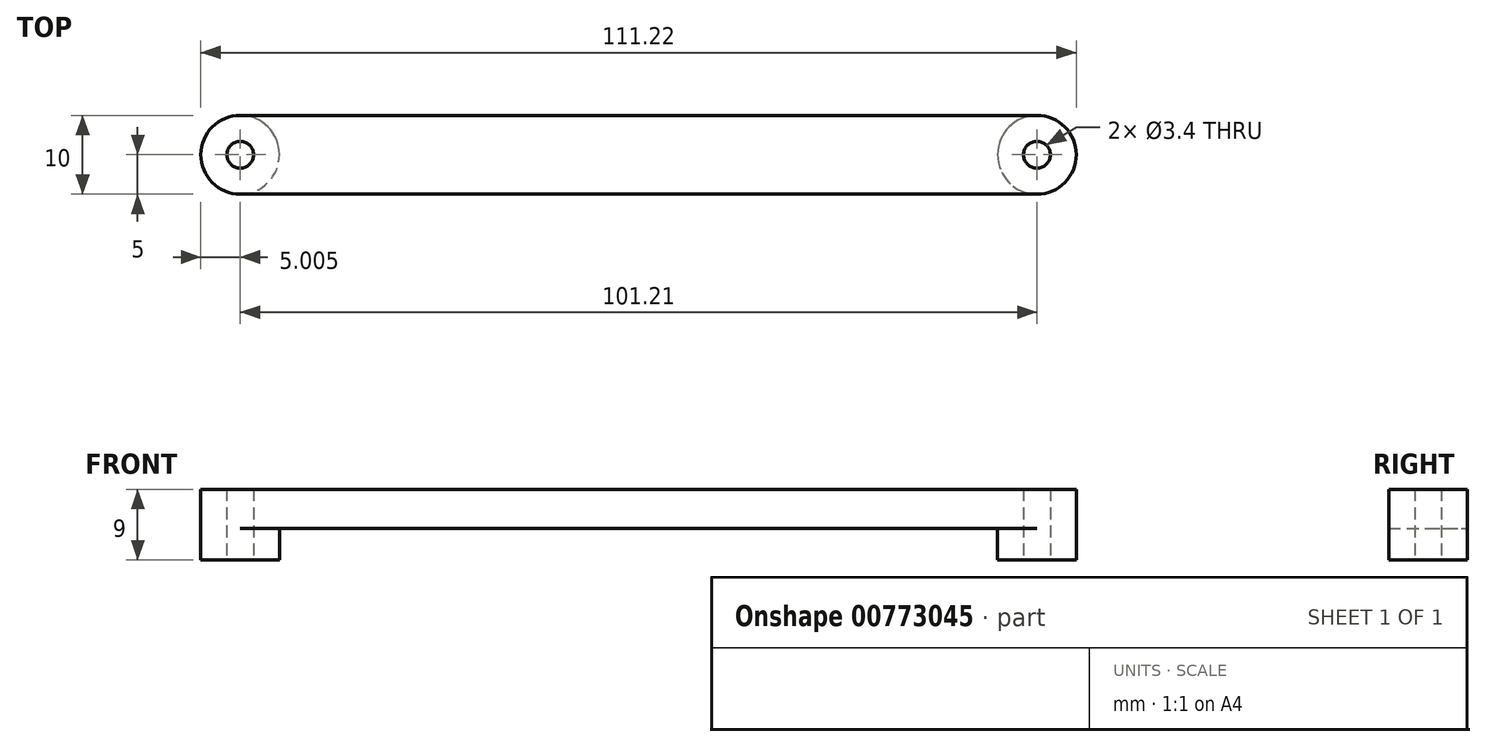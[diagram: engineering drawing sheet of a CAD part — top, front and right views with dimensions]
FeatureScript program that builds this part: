
annotation { "Feature Type Name" : "Feature", "Feature Type Description" : "" }
export const myFeature = defineFeature(function(context is Context, id is Id, definition is map)
    precondition{}
    {
        {
            var Q0;
            Q0=qCreatedBy(makeId("Top.planeOp"),FACE);
            var sketch = newSketch(context, id + "F0", { "sketchPlane" : qUnion([Q0])});
            skLineSegment(sketch, "E0.bottom", {"start": v(50.6, -5) * mm, "end": v(-50.6, -5) * mm});
            skLineSegment(sketch, "E0.top", {"start": v(50.6, 5) * mm, "end": v(-50.6, 5) * mm});
            skPoint(sketch, "E0.middle", {"position": v(0, 0) * mm});
            skArc(sketch, "E1", {"start": v(-50.6, -5) * mm, "mid": v(-55.6, 0) * mm, "end": v(-50.6, 5) * mm});
            skArc(sketch, "E2", {"start": v(50.6, 5) * mm, "mid": v(55.6, 0) * mm, "end": v(50.6, -5) * mm});
            skCircle(sketch, "E3", {"center": v(-50.6, 0) * mm, "radius": 1.7 * mm});
            skCircle(sketch, "E4", {"center": v(50.6, 0) * mm, "radius": 1.7 * mm});
            skSolve(sketch);
        }
        {
            var Q0;
            Q0 = qSketchRegion(id + "F0", true);
            extrude(context, id + "F1", {"entities" : qUnion([Q0]), "depth" : 5 * mm, "offsetDistance" : 25 * mm});
        }
        {
            var Q0;
            Q0=makeQuery(id+"F1.opExtrude","CAP_FACE",FACE,{"disambiguationData":[OSD([sQuery(id+"F0.wireOp",EDGE,"E0.bottom"),sQuery(id+"F0.wireOp",EDGE,"E0.top"),sQuery(id+"F0.wireOp",EDGE,"E1"),sQuery(id+"F0.wireOp",EDGE,"E2"),sQuery(id+"F0.wireOp",EDGE,"E3"),sQuery(id+"F0.wireOp",EDGE,"E4")])],"isStart":true});
            var sketch = newSketch(context, id + "F2", { "sketchPlane" : qUnion([Q0])});
            skCircle(sketch, "E5", {"center": v(-50.6, 0) * mm, "radius": 5 * mm});
            skCircle(sketch, "E6.0", {"center": v(-50.6, 0) * mm, "radius": 1.7 * mm});
            skSolve(sketch);
        }
        {
            var Q0;
            Q0 = qSketchRegion(id + "F2", true);
            extrude(context, id + "F3", {"entities" : qUnion([Q0]), "operationType" : NewBodyOperationType.ADD, "depth" : 4 * mm, "offsetDistance" : 25 * mm});
        }
        {
            var Q0;
            Q0=makeQuery(id+"F1.opExtrude","SWEPT_BODY",BODY,{"disambiguationData":[OSD([sQuery(id+"F0.wireOp",EDGE,"E0.bottom"),sQuery(id+"F0.wireOp",EDGE,"E0.top"),sQuery(id+"F0.wireOp",EDGE,"E1"),sQuery(id+"F0.wireOp",EDGE,"E2"),sQuery(id+"F0.wireOp",EDGE,"E3"),sQuery(id+"F0.wireOp",EDGE,"E4")])]});
            var Q1;
            Q1=qCreatedBy(makeId("Right.planeOp"),FACE);
            mirror(context, id + "F4", {"operationType" : NewBodyOperationType.ADD, "entities" : qUnion([Q0]), "mirrorPlane" : qUnion([Q1])});
        }
    });
